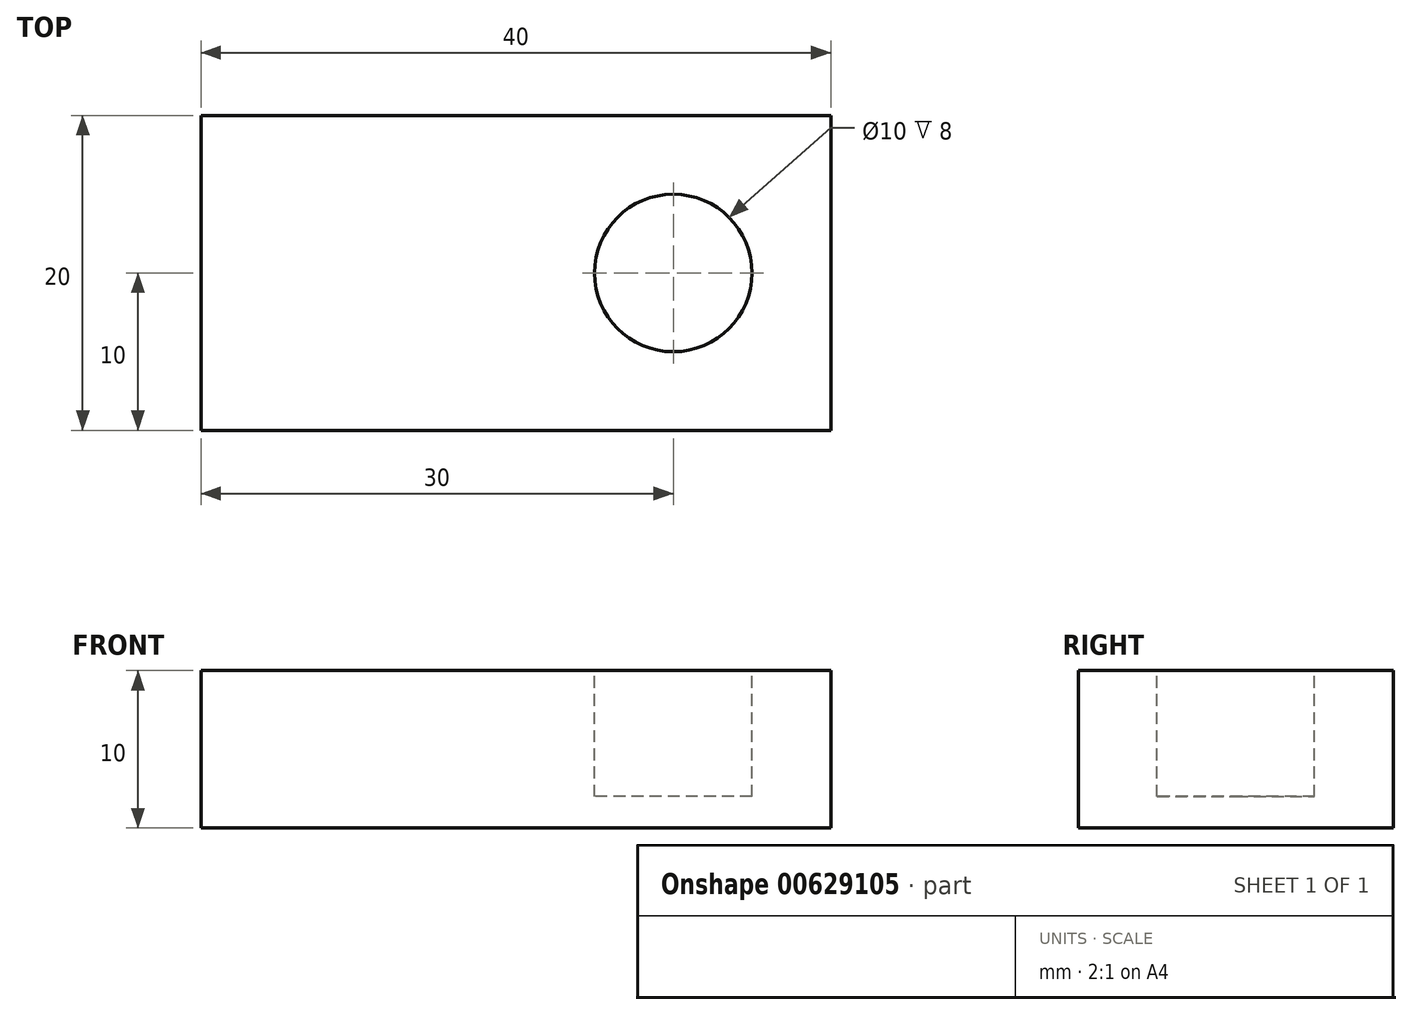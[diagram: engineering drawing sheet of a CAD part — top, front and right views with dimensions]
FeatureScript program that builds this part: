
annotation { "Feature Type Name" : "Feature", "Feature Type Description" : "" }
export const myFeature = defineFeature(function(context is Context, id is Id, definition is map)
    precondition{}
    {
        {
            var Q0;
            Q0=qCreatedBy(makeId("Top.planeOp"),FACE);
            var sketch = newSketch(context, id + "F0", { "sketchPlane" : qUnion([Q0])});
            skLineSegment(sketch, "E0.bottom", {"start": v(-30, 10) * mm, "end": v(10, 10) * mm});
            skLineSegment(sketch, "E0.top", {"start": v(-30, -10) * mm, "end": v(10, -10) * mm});
            skLineSegment(sketch, "E0.left", {"start": v(-30, 10) * mm, "end": v(-30, -10) * mm});
            skLineSegment(sketch, "E0.right", {"start": v(10, 10) * mm, "end": v(10, -10) * mm});
            skSolve(sketch);
        }
        {
            var Q0;
            Q0 = qSketchRegion(id + "F0", true);
            extrude(context, id + "F1", {"entities" : qUnion([Q0]), "depth" : 10 * mm, "offsetDistance" : 25 * mm});
        }
        {
            var Q0;
            Q0=makeQuery(id+"F1.opExtrude","CAP_FACE",FACE,{"disambiguationData":[OSD([sQuery(id+"F0.wireOp",EDGE,"E0.bottom"),sQuery(id+"F0.wireOp",EDGE,"E0.top"),sQuery(id+"F0.wireOp",EDGE,"E0.left"),sQuery(id+"F0.wireOp",EDGE,"E0.right")])],"isStart":false});
            var sketch = newSketch(context, id + "F2", { "sketchPlane" : qUnion([Q0])});
            skCircle(sketch, "E1", {"center": v(0, 0) * mm, "radius": 5 * mm});
            skSolve(sketch);
        }
        {
            var Q0;
            Q0=makeQuery(id+"F2.imprint","IMPRINT",FACE,{"disambiguationData":[TD([[makeQuery(id+"F2.imprint","IMPRINT",EDGE,{"derivedFrom":sQuery(id+"F2.wireOp",EDGE,"E1")}),1.0]])]});
            extrude(context, id + "F3", {"entities" : qUnion([Q0]), "operationType" : NewBodyOperationType.REMOVE, "oppositeDirection" : true, "depth" : 8 * mm, "offsetDistance" : 25 * mm});
        }
    });
